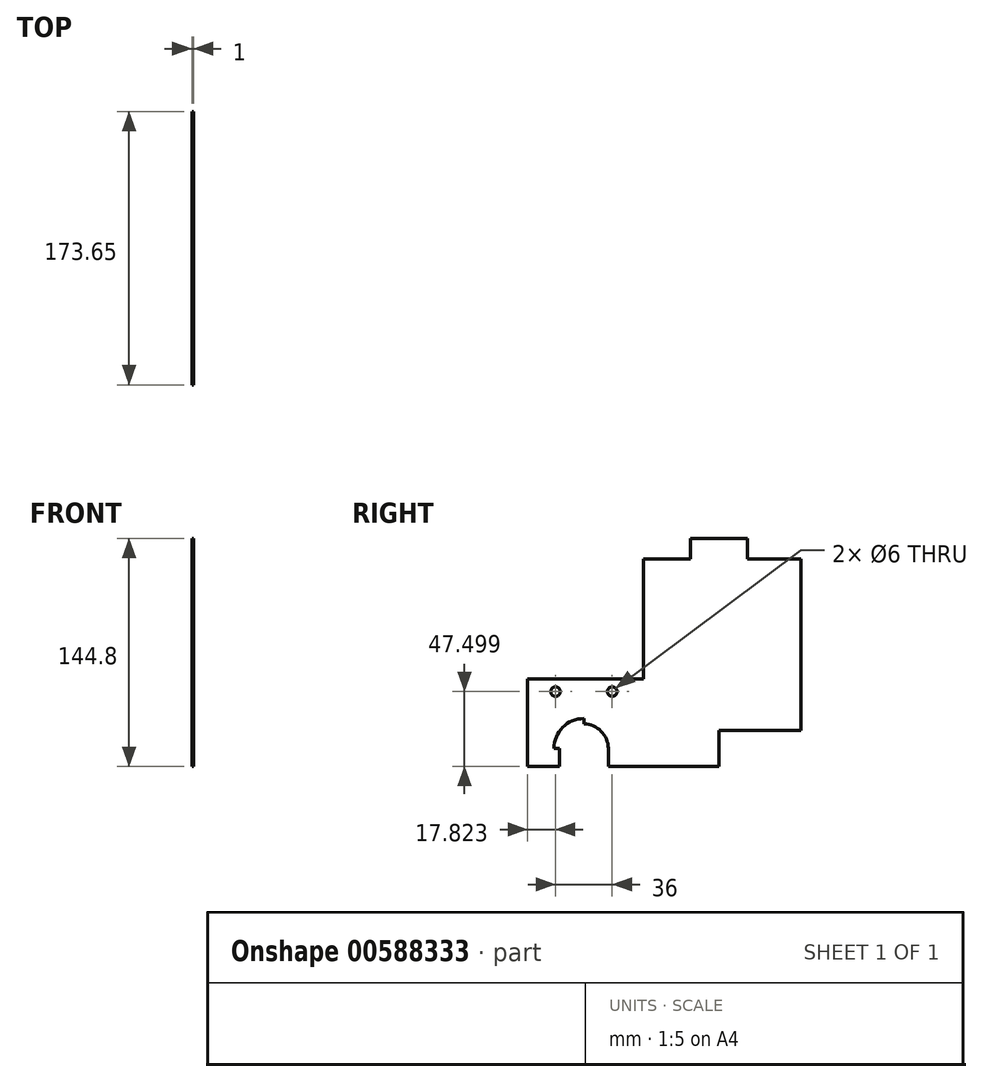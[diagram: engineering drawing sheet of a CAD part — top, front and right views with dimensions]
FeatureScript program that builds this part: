
annotation { "Feature Type Name" : "Feature", "Feature Type Description" : "" }
export const myFeature = defineFeature(function(context is Context, id is Id, definition is map)
    precondition{}
    {
        {
            var Q0;
            Q0=qCreatedBy(makeId("Right.planeOp"),FACE);
            var sketch = newSketch(context, id + "F0", { "sketchPlane" : qUnion([Q0])});
            skLineSegment(sketch, "E0.bottom", {"start": v(149.99, -16.92) * mm, "end": v(110.69, -16.92) * mm});
            skLineSegment(sketch, "E1", {"start": v(253.99, -16.92) * mm, "end": v(253.99, 15.83) * mm});
            skLineSegment(sketch, "E2", {"start": v(149.99, -16.92) * mm, "end": v(253.99, -16.92) * mm});
            skLineSegment(sketch, "E3", {"start": v(110.69, -16.92) * mm, "end": v(68.69, -16.92) * mm});
            skLineSegment(sketch, "E4", {"start": v(6.69, -16.92) * mm, "end": v(6.69, 15.83) * mm});
            skLineSegment(sketch, "E5", {"start": v(6.69, 15.83) * mm, "end": v(6.69, 88.83) * mm});
            skLineSegment(sketch, "E6", {"start": v(253.99, 15.83) * mm, "end": v(253.99, 88.83) * mm});
            skLineSegment(sketch, "E7", {"start": v(6.69, -16.92) * mm, "end": v(6.69, -39.67) * mm});
            skLineSegment(sketch, "E8", {"start": v(68.69, -28.3) * mm, "end": v(68.69, -16.92) * mm});
            skLineSegment(sketch, "E9", {"start": v(214.69, 92.03) * mm, "end": v(226.69, 92.03) * mm});
            skLineSegment(sketch, "E10", {"start": v(130.34, 105.13) * mm, "end": v(148.34, 105.13) * mm});
            skLineSegment(sketch, "E11", {"start": v(130.34, 150.13) * mm, "end": v(148.34, 132.13) * mm});
            skLineSegment(sketch, "E12", {"start": v(226.69, 92.03) * mm, "end": v(253.99, 92.03) * mm});
            skLineSegment(sketch, "E13", {"start": v(214.69, 92.03) * mm, "end": v(148.34, 92.03) * mm});
            skLineSegment(sketch, "E14", {"start": v(148.34, 105.13) * mm, "end": v(148.34, 102.13) * mm});
            skLineSegment(sketch, "E15", {"start": v(112.34, 105.13) * mm, "end": v(112.34, 102.13) * mm});
            skLineSegment(sketch, "E16", {"start": v(143.34, 132.13) * mm, "end": v(143.34, 105.13) * mm});
            skLineSegment(sketch, "E17", {"start": v(117.34, 132.13) * mm, "end": v(143.34, 132.13) * mm});
            skLineSegment(sketch, "E18", {"start": v(6.69, -39.67) * mm, "end": v(6.69, -7.34) * mm});
            skLineSegment(sketch, "E19", {"start": v(6.69, -16.92) * mm, "end": v(6.69, -28.3) * mm});
            skLineSegment(sketch, "E20", {"start": v(68.69, -16.92) * mm, "end": v(68.69, 15.83) * mm});
            skLineSegment(sketch, "E21", {"start": v(68.69, 15.83) * mm, "end": v(6.69, 15.83) * mm});
            skLineSegment(sketch, "E22", {"start": v(253.99, 88.83) * mm, "end": v(253.99, 92.03) * mm});
            skLineSegment(sketch, "E23", {"start": v(6.69, 88.83) * mm, "end": v(6.69, 92.03) * mm});
            skLineSegment(sketch, "E24", {"start": v(136.34, 56.93) * mm, "end": v(124.34, 56.93) * mm});
            skLineSegment(sketch, "E25", {"start": v(124.34, 56.93) * mm, "end": v(124.34, 28.93) * mm});
            skLineSegment(sketch, "E26", {"start": v(124.34, 28.93) * mm, "end": v(136.34, 28.93) * mm});
            skLineSegment(sketch, "E27", {"start": v(136.34, 56.93) * mm, "end": v(136.34, 28.93) * mm});
            skLineSegment(sketch, "E28", {"start": v(124.34, 28.93) * mm, "end": v(124.34, 27.53) * mm});
            skLineSegment(sketch, "E29", {"start": v(124.34, 27.53) * mm, "end": v(124.34, 24.73) * mm});
            skLineSegment(sketch, "E30", {"start": v(124.34, 24.73) * mm, "end": v(124.34, 21.93) * mm});
            skLineSegment(sketch, "E31", {"start": v(124.34, 21.93) * mm, "end": v(124.34, 19.13) * mm});
            skLineSegment(sketch, "E32", {"start": v(124.34, 19.13) * mm, "end": v(136.34, 19.13) * mm});
            skLineSegment(sketch, "E33", {"start": v(136.34, 19.13) * mm, "end": v(136.34, 28.93) * mm});
            skLineSegment(sketch, "E34", {"start": v(124.34, 19.13) * mm, "end": v(124.34, -8.87) * mm});
            skLineSegment(sketch, "E35", {"start": v(124.34, -8.87) * mm, "end": v(136.34, -8.87) * mm});
            skLineSegment(sketch, "E36", {"start": v(136.34, -8.87) * mm, "end": v(136.34, 19.13) * mm});
            skLineSegment(sketch, "E37", {"start": v(6.69, 92.03) * mm, "end": v(110.69, 92.03) * mm});
            skLineSegment(sketch, "E38", {"start": v(110.69, 92.03) * mm, "end": v(110.69, -16.92) * mm});
            skLineSegment(sketch, "E39", {"start": v(253.99, 92.03) * mm, "end": v(226.69, 92.03) * mm});
            skLineSegment(sketch, "E40", {"start": v(149.99, -16.92) * mm, "end": v(149.99, 92.03) * mm});
            skPoint(sketch, "E41.trimOffspring.start.orphan", {"position": v(201.99, 37.55) * mm});
            skLineSegment(sketch, "E42.trimOffspring", {"start": v(214.69, 92.03) * mm, "end": v(179.88, 92.03) * mm});
            skPoint(sketch, "E43.end.orphan", {"position": v(201.99, 92.03) * mm});
            skPoint(sketch, "E44.orphan", {"position": v(58.69, 37.55) * mm});
            skPoint(sketch, "E45.end.orphan", {"position": v(58.69, 92.03) * mm});
            skLineSegment(sketch, "E46", {"start": v(136.34, 56.93) * mm, "end": v(136.34, 68.03) * mm});
            skLineSegment(sketch, "E47", {"start": v(136.34, 68.03) * mm, "end": v(124.34, 68.03) * mm});
            skLineSegment(sketch, "E48", {"start": v(124.34, 68.03) * mm, "end": v(124.34, 92.03) * mm});
            skLineSegment(sketch, "E49", {"start": v(124.34, 92.03) * mm, "end": v(136.34, 92.03) * mm});
            skLineSegment(sketch, "E50.trimOffspring", {"start": v(112.34, 92.03) * mm, "end": v(6.69, 92.03) * mm});
            skLineSegment(sketch, "E51", {"start": v(136.34, 92.03) * mm, "end": v(136.34, 68.03) * mm});
            skPoint(sketch, "E52.end.orphan", {"position": v(78.84, 150.13) * mm});
            skLineSegment(sketch, "E53", {"start": v(130.34, 105.13) * mm, "end": v(130.34, 102.13) * mm});
            skLineSegment(sketch, "E54", {"start": v(130.34, -53.63) * mm, "end": v(82.34, -53.63) * mm});
            skLineSegment(sketch, "E55", {"start": v(82.34, -53.63) * mm, "end": v(130.34, -53.63) * mm});
            skLineSegment(sketch, "E56", {"start": v(130.34, -53.63) * mm, "end": v(178.34, -53.63) * mm});
            skLineSegment(sketch, "E57", {"start": v(178.34, -16.92) * mm, "end": v(178.34, 92.03) * mm});
            skLineSegment(sketch, "E58", {"start": v(82.34, 92.03) * mm, "end": v(82.34, -16.92) * mm});
            skLineSegment(sketch, "E59", {"start": v(148.34, 132.13) * mm, "end": v(155.59, 124.88) * mm});
            skLineSegment(sketch, "E60", {"start": v(105.09, 124.88) * mm, "end": v(112.34, 132.13) * mm});
            skLineSegment(sketch, "E61", {"start": v(179.88, 92.03) * mm, "end": v(178.34, 92.03) * mm});
            skLineSegment(sketch, "E62", {"start": v(110.69, 92.03) * mm, "end": v(82.34, 92.03) * mm});
            skLineSegment(sketch, "E63", {"start": v(216.16, 88.83) * mm, "end": v(216.16, 92.03) * mm});
            skLineSegment(sketch, "E64", {"start": v(208.99, 88.83) * mm, "end": v(209.16, 88.83) * mm});
            skPoint(sketch, "E65.start.orphan", {"position": v(201.99, 88.83) * mm});
            skLineSegment(sketch, "E66", {"start": v(68.69, 15.83) * mm, "end": v(82.34, 15.83) * mm});
            skPoint(sketch, "E67.end.orphan", {"position": v(178.34, -16.92) * mm});
            skPoint(sketch, "E67.start.orphan", {"position": v(216.16, 37.55) * mm});
            skLineSegment(sketch, "E68", {"start": v(178.34, -16.92) * mm, "end": v(182.34, -16.92) * mm});
            skLineSegment(sketch, "E69", {"start": v(182.34, -16.92) * mm, "end": v(182.34, 92.03) * mm});
            skLineSegment(sketch, "E70", {"start": v(82.34, 92.03) * mm, "end": v(78.34, 92.03) * mm});
            skLineSegment(sketch, "E71", {"start": v(78.34, 92.03) * mm, "end": v(78.34, -16.92) * mm});
            skLineSegment(sketch, "E72", {"start": v(223.16, 88.83) * mm, "end": v(225.16, 88.83) * mm});
            skLineSegment(sketch, "E73", {"start": v(225.16, 88.83) * mm, "end": v(225.16, 78.83) * mm});
            skLineSegment(sketch, "E74", {"start": v(225.16, 78.83) * mm, "end": v(223.16, 78.83) * mm});
            skLineSegment(sketch, "E75.bottom", {"start": v(225.16, 88.83) * mm, "end": v(223.16, 88.83) * mm});
            skPoint(sketch, "E76.start.orphan", {"position": v(37.69, 15.83) * mm});
            skLineSegment(sketch, "E77", {"start": v(6.69, 15.83) * mm, "end": v(6.69, 18.63) * mm});
            skLineSegment(sketch, "E78", {"start": v(6.69, 18.63) * mm, "end": v(6.69, 21.43) * mm});
            skLineSegment(sketch, "E79", {"start": v(6.69, 21.43) * mm, "end": v(6.69, 24.23) * mm});
            skLineSegment(sketch, "E80", {"start": v(6.69, 24.23) * mm, "end": v(6.69, 27.03) * mm});
            skLineSegment(sketch, "E81", {"start": v(6.69, 27.03) * mm, "end": v(6.69, 29.83) * mm});
            skLineSegment(sketch, "E82", {"start": v(6.69, 29.83) * mm, "end": v(6.69, 32.63) * mm});
            skLineSegment(sketch, "E83", {"start": v(6.69, 32.63) * mm, "end": v(37.69, 32.63) * mm});
            skLineSegment(sketch, "E84", {"start": v(68.69, 15.83) * mm, "end": v(54.69, 15.83) * mm});
            skLineSegment(sketch, "E85", {"start": v(37.69, 32.63) * mm, "end": v(33.19, 32.63) * mm});
            skLineSegment(sketch, "E86.trimOffspring", {"start": v(37.69, 44.63) * mm, "end": v(37.69, 92.03) * mm});
            skLineSegment(sketch, "E87", {"start": v(130.34, -16.92) * mm, "end": v(149.99, -16.92) * mm});
            skLineSegment(sketch, "E88", {"start": v(68.69, -28.3) * mm, "end": v(82.34, -28.3) * mm});
            skLineSegment(sketch, "E89", {"start": v(82.34, -28.3) * mm, "end": v(82.34, -16.92) * mm});
            skLineSegment(sketch, "E90.trimOffspring", {"start": v(37.69, 15.83) * mm, "end": v(37.69, 32.63) * mm});
            skLineSegment(sketch, "E91", {"start": v(44.51, -6.23) * mm, "end": v(44.51, -12.8) * mm});
            skLineSegment(sketch, "E92", {"start": v(68.69, -28.3) * mm, "end": v(60.01, -28.3) * mm});
            skArc(sketch, "E93", {"start": v(60.01, -28.3) * mm, "mid": v(44.51, -12.8) * mm, "end": v(29.01, -28.3) * mm});
            skArc(sketch, "E94", {"start": v(63.51, -28.3) * mm, "mid": v(44.51, -9.3) * mm, "end": v(25.51, -28.3) * mm});
            skLineSegment(sketch, "E95", {"start": v(29.51, 7.83) * mm, "end": v(26.51, 7.83) * mm});
            skLineSegment(sketch, "E96", {"start": v(59.51, 7.83) * mm, "end": v(62.51, 7.83) * mm});
            skCircle(sketch, "E97", {"center": v(62.51, 7.83) * mm, "radius": 3 * mm});
            skCircle(sketch, "E98", {"center": v(26.51, 7.83) * mm, "radius": 3 * mm});
            skLineSegment(sketch, "E99", {"start": v(44.51, 7.83) * mm, "end": v(44.51, 15.83) * mm});
            skLineSegment(sketch, "E100", {"start": v(44.51, 32.63) * mm, "end": v(61.86, 32.63) * mm});
            skLineSegment(sketch, "E101", {"start": v(44.51, 15.83) * mm, "end": v(44.51, 32.63) * mm});
            skLineSegment(sketch, "E102", {"start": v(44.51, 32.63) * mm, "end": v(40.01, 32.63) * mm});
            skLineSegment(sketch, "E103", {"start": v(253.99, 92.03) * mm, "end": v(251.99, 92.03) * mm});
            skLineSegment(sketch, "E104", {"start": v(251.99, 92.03) * mm, "end": v(251.99, -16.92) * mm});
            skLineSegment(sketch, "E105", {"start": v(82.34, -16.92) * mm, "end": v(82.34, -39.67) * mm});
            skLineSegment(sketch, "E106", {"start": v(253.99, -16.92) * mm, "end": v(253.99, -39.67) * mm});
            skLineSegment(sketch, "E107", {"start": v(253.99, -39.67) * mm, "end": v(82.34, -39.67) * mm});
            skLineSegment(sketch, "E108", {"start": v(112.34, 107.13) * mm, "end": v(112.34, 105.13) * mm});
            skLineSegment(sketch, "E109", {"start": v(148.34, 107.13) * mm, "end": v(148.34, 105.13) * mm});
            skLineSegment(sketch, "E110", {"start": v(6.69, -39.67) * mm, "end": v(29.01, -39.67) * mm});
            skLineSegment(sketch, "E111", {"start": v(29.01, -28.3) * mm, "end": v(29.01, -39.67) * mm});
            skLineSegment(sketch, "E112", {"start": v(60.01, -28.3) * mm, "end": v(60.01, -39.67) * mm});
            skLineSegment(sketch, "E113.trimOffspring", {"start": v(29.01, -28.3) * mm, "end": v(6.69, -28.3) * mm});
            skLineSegment(sketch, "E114.trimOffspring", {"start": v(29.01, -28.3) * mm, "end": v(28.84, -28.3) * mm});
            skLineSegment(sketch, "E115.trimOffspring", {"start": v(60.01, -39.67) * mm, "end": v(82.34, -39.67) * mm});
            skLineSegment(sketch, "E116", {"start": v(6.69, 92.03) * mm, "end": v(8.69, 92.03) * mm});
            skLineSegment(sketch, "E117", {"start": v(8.69, 92.03) * mm, "end": v(8.69, -39.67) * mm});
            skLineSegment(sketch, "E118", {"start": v(251.99, -16.92) * mm, "end": v(251.99, -39.67) * mm});
            skLineSegment(sketch, "E119", {"start": v(148.34, 105.13) * mm, "end": v(148.34, 107.13) * mm});
            skLineSegment(sketch, "E120", {"start": v(148.34, 107.13) * mm, "end": v(147.34, 107.13) * mm});
            skLineSegment(sketch, "E121", {"start": v(147.34, 107.13) * mm, "end": v(147.34, 132.13) * mm});
            skLineSegment(sketch, "E122", {"start": v(147.34, 132.13) * mm, "end": v(148.34, 132.13) * mm});
            skLineSegment(sketch, "E123", {"start": v(112.34, 105.13) * mm, "end": v(112.34, 107.13) * mm});
            skLineSegment(sketch, "E124", {"start": v(112.34, 107.13) * mm, "end": v(113.34, 107.13) * mm});
            skLineSegment(sketch, "E125", {"start": v(113.34, 107.13) * mm, "end": v(113.34, 132.13) * mm});
            skLineSegment(sketch, "E126", {"start": v(112.34, 132.13) * mm, "end": v(113.34, 132.13) * mm});
            skLineSegment(sketch, "E127.trimOffspring", {"start": v(130.34, 92.03) * mm, "end": v(130.34, -53.63) * mm});
            skPoint(sketch, "E128.start.orphan", {"position": v(117.34, 132.13) * mm});
            skLineSegment(sketch, "E129", {"start": v(130.34, 92.03) * mm, "end": v(148.34, 92.03) * mm});
            skLineSegment(sketch, "E130", {"start": v(148.34, 92.03) * mm, "end": v(148.34, 105.13) * mm});
            skLineSegment(sketch, "E131", {"start": v(148.34, 105.13) * mm, "end": v(112.34, 105.13) * mm});
            skLineSegment(sketch, "E132", {"start": v(112.34, 105.13) * mm, "end": v(112.34, 92.03) * mm});
            skSolve(sketch);
        }
        {
            var Q0;
            {var subQ4=sQuery(id+"F0.wireOp",EDGE,"E39");Q0=makeQuery(id+"F0.imprint","IMPRINT",FACE,{"disambiguationData":[TD([[makeQuery(id+"F0.imprint","IMPRINT",EDGE,{"derivedFrom":subQ4}),1.0]])]});}
            var Q1;
            {var subQ0=sQuery(id+"F0.wireOp",EDGE,"E68");Q1=makeQuery(id+"F0.imprint","IMPRINT",FACE,{"disambiguationData":[TD([[makeQuery(id+"F0.imprint","IMPRINT",EDGE,{"derivedFrom":subQ0}),-1.0]])]});}
            var Q2;
            Q2=makeQuery(id+"F0.imprint","IMPRINT",FACE,{"disambiguationData":[TD([[makeQuery(id+"F0.imprint","IMPRINT",EDGE,{"derivedFrom":sQuery(id+"F0.wireOp",EDGE,"E57")}),-1.0]])]});
            var Q3;
            {var subQ0=sQuery(id+"F0.wireOp",EDGE,"E40");Q3=makeQuery(id+"F0.imprint","IMPRINT",FACE,{"disambiguationData":[TD([[makeQuery(id+"F0.imprint","IMPRINT",EDGE,{"derivedFrom":subQ0}),-1.0]])]});}
            var Q4;
            Q4=makeQuery(id+"F0.imprint","IMPRINT",FACE,{"disambiguationData":[TD([[makeQuery(id+"F0.imprint","IMPRINT",EDGE,{"derivedFrom":sQuery(id+"F0.wireOp",EDGE,"E27")}),1.0]])]});
            var Q5;
            {var subQ1=sQuery(id+"F0.wireOp",EDGE,"E0.bottom");Q5=makeQuery(id+"F0.imprint","IMPRINT",FACE,{"disambiguationData":[TD([[makeQuery(id+"F0.imprint","IMPRINT",EDGE,{"derivedFrom":subQ1}),1.0]])]});}
            var Q6;
            {var subQ4=sQuery(id+"F0.wireOp",EDGE,"E0.bottom");Q6=makeQuery(id+"F0.imprint","IMPRINT",FACE,{"disambiguationData":[TD([[makeQuery(id+"F0.imprint","IMPRINT",EDGE,{"derivedFrom":subQ4}),-1.0]])]});}
            var Q7;
            {var subQ0=sQuery(id+"F0.wireOp",EDGE,"E36");Q7=makeQuery(id+"F0.imprint","IMPRINT",FACE,{"disambiguationData":[TD([[makeQuery(id+"F0.imprint","IMPRINT",EDGE,{"derivedFrom":subQ0}),1.0]])]});}
            var Q8;
            {var subQ0=sQuery(id+"F0.wireOp",EDGE,"E34");Q8=makeQuery(id+"F0.imprint","IMPRINT",FACE,{"disambiguationData":[TD([[makeQuery(id+"F0.imprint","IMPRINT",EDGE,{"derivedFrom":subQ0}),1.0]])]});}
            var Q9;
            {var subQ0=sQuery(id+"F0.wireOp",EDGE,"E33");Q9=makeQuery(id+"F0.imprint","IMPRINT",FACE,{"disambiguationData":[TD([[makeQuery(id+"F0.imprint","IMPRINT",EDGE,{"derivedFrom":subQ0}),1.0]])]});}
            var Q10;
            {var subQ0=sQuery(id+"F0.wireOp",EDGE,"E28");Q10=makeQuery(id+"F0.imprint","IMPRINT",FACE,{"disambiguationData":[TD([[makeQuery(id+"F0.imprint","IMPRINT",EDGE,{"derivedFrom":subQ0}),1.0]])]});}
            var Q11;
            {var subQ0=sQuery(id+"F0.wireOp",EDGE,"E27");Q11=makeQuery(id+"F0.imprint","IMPRINT",FACE,{"disambiguationData":[TD([[makeQuery(id+"F0.imprint","IMPRINT",EDGE,{"derivedFrom":subQ0}),-1.0]])]});}
            var Q12;
            {var subQ0=sQuery(id+"F0.wireOp",EDGE,"E25");Q12=makeQuery(id+"F0.imprint","IMPRINT",FACE,{"disambiguationData":[TD([[makeQuery(id+"F0.imprint","IMPRINT",EDGE,{"derivedFrom":subQ0}),1.0]])]});}
            var Q13;
            {var subQ0=sQuery(id+"F0.wireOp",EDGE,"E46");Q13=makeQuery(id+"F0.imprint","IMPRINT",FACE,{"disambiguationData":[TD([[makeQuery(id+"F0.imprint","IMPRINT",EDGE,{"derivedFrom":subQ0}),1.0]])]});}
            var Q14;
            {var subQ0=sQuery(id+"F0.wireOp",EDGE,"E51");Q14=makeQuery(id+"F0.imprint","IMPRINT",FACE,{"disambiguationData":[TD([[makeQuery(id+"F0.imprint","IMPRINT",EDGE,{"derivedFrom":subQ0}),-1.0]])]});}
            var Q15;
            {var subQ0=sQuery(id+"F0.wireOp",EDGE,"E48");Q15=makeQuery(id+"F0.imprint","IMPRINT",FACE,{"disambiguationData":[TD([[makeQuery(id+"F0.imprint","IMPRINT",EDGE,{"derivedFrom":subQ0}),-1.0]])]});}
            var Q16;
            {var subQ5=sQuery(id+"F0.wireOp",EDGE,"E38");Q16=makeQuery(id+"F0.imprint","IMPRINT",FACE,{"disambiguationData":[TD([[makeQuery(id+"F0.imprint","IMPRINT",EDGE,{"derivedFrom":subQ5}),-1.0]])]});}
            var Q17;
            {var subQ0=sQuery(id+"F0.wireOp",EDGE,"E58");var subQ5=sQuery(id+"F0.wireOp",EDGE,"E66");var subQ6=makeQuery(id+"F0.imprint","INTERSECT",VERTEX,{"derivedFrom":[subQ0,subQ5]});Q17=makeQuery(id+"F0.imprint","IMPRINT",FACE,{"disambiguationData":[TD([[makeQuery(id+"F0.imprint","IMPRINT",EDGE,{"disambiguationData":[TD([[subQ6,1.0]])],"derivedFrom":subQ5}),-1.0]])]});}
            var Q18;
            {var subQ0=sQuery(id+"F0.wireOp",EDGE,"E20");Q18=makeQuery(id+"F0.imprint","IMPRINT",FACE,{"disambiguationData":[TD([[makeQuery(id+"F0.imprint","IMPRINT",EDGE,{"derivedFrom":subQ0}),-1.0]])]});}
            var Q19;
            {var subQ1=sQuery(id+"F0.wireOp",EDGE,"E8");Q19=makeQuery(id+"F0.imprint","IMPRINT",FACE,{"disambiguationData":[TD([[makeQuery(id+"F0.imprint","IMPRINT",EDGE,{"derivedFrom":subQ1}),-1.0]])]});}
            var Q20;
            {var subQ1=sQuery(id+"F0.wireOp",EDGE,"E88");Q20=makeQuery(id+"F0.imprint","IMPRINT",FACE,{"disambiguationData":[TD([[makeQuery(id+"F0.imprint","IMPRINT",EDGE,{"derivedFrom":subQ1}),-1.0]])]});}
            var Q21;
            {var subQ12=sQuery(id+"F0.wireOp",EDGE,"E8");Q21=makeQuery(id+"F0.imprint","IMPRINT",FACE,{"disambiguationData":[TD([[makeQuery(id+"F0.imprint","IMPRINT",EDGE,{"derivedFrom":subQ12}),1.0]])]});}
            var Q22;
            {var subQ0=sQuery(id+"F0.wireOp",EDGE,"E93");var subQ1=sQuery(id+"F0.wireOp",EDGE,"E91");var subQ2=makeQuery(id+"F0.imprint","INTERSECT",VERTEX,{"derivedFrom":[subQ1,subQ0]});Q22=makeQuery(id+"F0.imprint","IMPRINT",FACE,{"disambiguationData":[TD([[makeQuery(id+"F0.imprint","IMPRINT",EDGE,{"disambiguationData":[TD([[subQ2,1.0]])],"derivedFrom":subQ1}),1.0]])]});}
            var Q23;
            {var subQ10=sQuery(id+"F0.wireOp",EDGE,"E84");Q23=makeQuery(id+"F0.imprint","IMPRINT",FACE,{"disambiguationData":[TD([[makeQuery(id+"F0.imprint","IMPRINT",EDGE,{"derivedFrom":subQ10}),-1.0]])]});}
            var Q24;
            {var subQ0=sQuery(id+"F0.wireOp",EDGE,"E70");Q24=makeQuery(id+"F0.imprint","IMPRINT",FACE,{"disambiguationData":[TD([[makeQuery(id+"F0.imprint","IMPRINT",EDGE,{"derivedFrom":subQ0}),1.0]])]});}
            var Q25;
            {var subQ0=sQuery(id+"F0.wireOp",EDGE,"E85");Q25=makeQuery(id+"F0.imprint","IMPRINT",FACE,{"disambiguationData":[TD([[makeQuery(id+"F0.imprint","IMPRINT",EDGE,{"derivedFrom":subQ0}),1.0]])]});}
            var Q26;
            {var subQ5=sQuery(id+"F0.wireOp",EDGE,"E111");Q26=makeQuery(id+"F0.imprint","IMPRINT",FACE,{"disambiguationData":[TD([[makeQuery(id+"F0.imprint","IMPRINT",EDGE,{"derivedFrom":subQ5}),-1.0]])]});}
            var Q27;
            {var subQ3=sQuery(id+"F0.wireOp",EDGE,"E114.trimOffspring");Q27=makeQuery(id+"F0.imprint","IMPRINT",FACE,{"disambiguationData":[TD([[makeQuery(id+"F0.imprint","IMPRINT",EDGE,{"derivedFrom":subQ3}),-1.0]])]});}
            var Q28;
            {var subQ5=sQuery(id+"F0.wireOp",EDGE,"E14");var subQ7=sQuery(id+"F0.wireOp",EDGE,"E13");var subQ8=makeQuery(id+"F0.imprint","INTERSECT",VERTEX,{"derivedFrom":[subQ7,subQ5]});Q28=makeQuery(id+"F0.imprint","IMPRINT",FACE,{"disambiguationData":[TD([[makeQuery(id+"F0.imprint","IMPRINT",EDGE,{"disambiguationData":[TD([[subQ8,1.0]])],"derivedFrom":subQ5}),-1.0]])]});}
            var Q29;
            {var subQ5=sQuery(id+"F0.wireOp",EDGE,"E50.trimOffspring");var subQ6=sQuery(id+"F0.wireOp",EDGE,"E15");var subQ7=makeQuery(id+"F0.imprint","INTERSECT",VERTEX,{"derivedFrom":[subQ6,subQ5]});Q29=makeQuery(id+"F0.imprint","IMPRINT",FACE,{"disambiguationData":[TD([[makeQuery(id+"F0.imprint","IMPRINT",EDGE,{"disambiguationData":[TD([[subQ7,1.0]])],"derivedFrom":subQ6}),1.0]])]});}
            var Q30;
            {var subQ3=sQuery(id+"F0.wireOp",EDGE,"dMi7BYDC-dX2N-1Bzj-NFyT-o7kfizO2VCdV");var subQ5=sQuery(id+"F0.wireOp",EDGE,"E14");var subQ7=makeQuery(id+"F0.imprint","INTERSECT",VERTEX,{"derivedFrom":[subQ5,subQ3]});Q30=makeQuery(id+"F0.imprint","IMPRINT",FACE,{"disambiguationData":[TD([[makeQuery(id+"F0.imprint","IMPRINT",EDGE,{"disambiguationData":[TD([[subQ7,-1.0]])],"derivedFrom":subQ3}),-1.0]])]});}
            var Q31;
            {var subQ3=sQuery(id+"F0.wireOp",EDGE,"dMi7BYDC-dX2N-1Bzj-NFyT-o7kfizO2VCdV");var subQ5=sQuery(id+"F0.wireOp",EDGE,"E15");var subQ7=makeQuery(id+"F0.imprint","INTERSECT",VERTEX,{"derivedFrom":[subQ5,subQ3]});Q31=makeQuery(id+"F0.imprint","IMPRINT",FACE,{"disambiguationData":[TD([[makeQuery(id+"F0.imprint","IMPRINT",EDGE,{"disambiguationData":[TD([[subQ7,1.0]])],"derivedFrom":subQ3}),-1.0]])]});}
            var Q32;
            Q32=makeQuery(id+"F0.imprint","IMPRINT",FACE,{"disambiguationData":[TD([[makeQuery(id+"F0.imprint","IMPRINT",EDGE,{"derivedFrom":sQuery(id+"F0.wireOp",EDGE,"fd439c25-8f7c-49bf-9d93-cb74bf624e18")}),1.0]])]});
            extrude(context, id + "F1", {"entities" : qUnion([Q0, Q1, Q2, Q3, Q4, Q5, Q6, Q7, Q8, Q9, Q10, Q11, Q12, Q13, Q14, Q15, Q16, Q17, Q18, Q19, Q20, Q21, Q22, Q23, Q24, Q25, Q26, Q27, Q28, Q29, Q30, Q31, Q32]), "depth" : 1 * mm, "offsetDistance" : 25 * mm});
        }
    });
